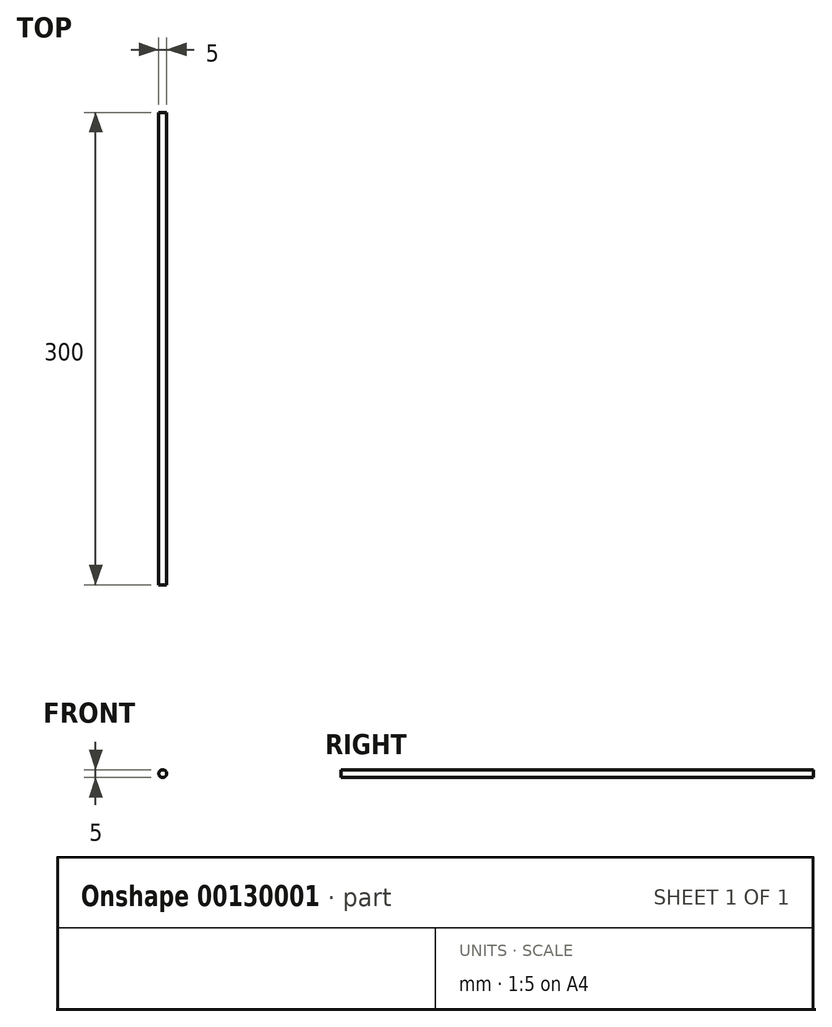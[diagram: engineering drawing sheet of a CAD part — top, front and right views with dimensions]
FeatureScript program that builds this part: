
annotation { "Feature Type Name" : "Feature", "Feature Type Description" : "" }
export const myFeature = defineFeature(function(context is Context, id is Id, definition is map)
    precondition{}
    {
        {
            var Q0;
            Q0=qCreatedBy(makeId("Front.planeOp"),FACE);
            var sketch = newSketch(context, id + "F0", { "sketchPlane" : qUnion([Q0])});
            skCircle(sketch, "E0", {"center": v(0, 0) * mm, "radius": 2.5 * mm});
            skSolve(sketch);
        }
        {
            var Q0;
            Q0 = qSketchRegion(id + "F0", true);
            extrude(context, id + "F1", {"entities" : qUnion([Q0]), "depth" : 300 * mm});
        }
    });
